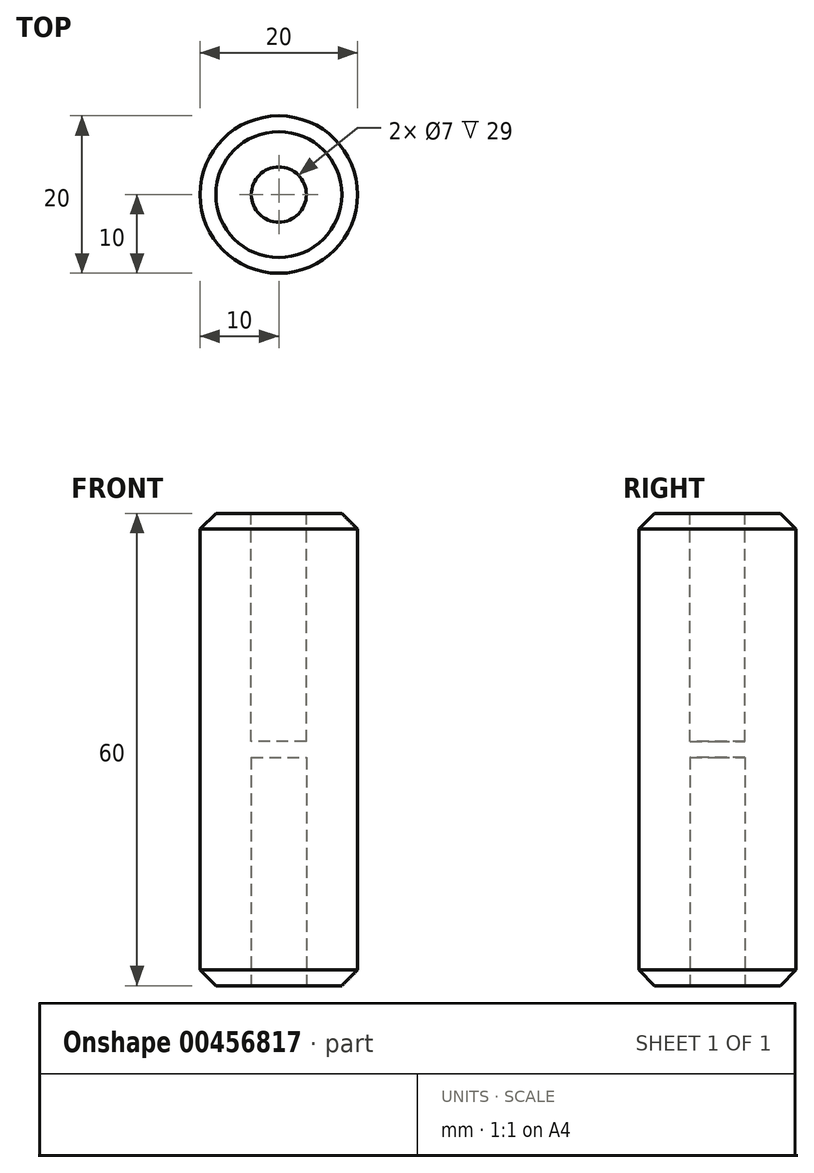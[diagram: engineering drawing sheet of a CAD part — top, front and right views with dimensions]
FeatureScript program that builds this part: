
annotation { "Feature Type Name" : "Feature", "Feature Type Description" : "" }
export const myFeature = defineFeature(function(context is Context, id is Id, definition is map)
    precondition{}
    {
        {
            var Q0;
            Q0=qCreatedBy(makeId("Top.planeOp"),FACE);
            var sketch = newSketch(context, id + "F0", { "sketchPlane" : qUnion([Q0])});
            skCircle(sketch, "E0", {"center": v(0, 0) * mm, "radius": 10 * mm});
            skSolve(sketch);
        }
        {
            var Q0;
            Q0=makeQuery(id+"F0.imprint","IMPRINT",FACE,{"disambiguationData":[TD([[makeQuery(id+"F0.imprint","IMPRINT",EDGE,{"derivedFrom":sQuery(id+"F0.wireOp",EDGE,"E0")}),1.0]])]});
            extrude(context, id + "F1", {"entities" : qUnion([Q0]), "endBound" : BoundingType.SYMMETRIC, "depth" : 60 * mm});
        }
        {
            var Q0;
            Q0=makeQuery(id+"F1.opExtrude","CAP_FACE",FACE,{"disambiguationData":[OSD([sQuery(id+"F0.wireOp",EDGE,"E0")])],"isStart":false});
            var sketch = newSketch(context, id + "F2", { "sketchPlane" : qUnion([Q0])});
            skCircle(sketch, "E1", {"center": v(0, 0) * mm, "radius": 3.5 * mm});
            skSolve(sketch);
        }
        {
            var Q0;
            Q0=makeQuery(id+"F1.opExtrude","CAP_FACE",FACE,{"disambiguationData":[OSD([sQuery(id+"F0.wireOp",EDGE,"E0")])],"isStart":true});
            var sketch = newSketch(context, id + "F3", { "sketchPlane" : qUnion([Q0])});
            skCircle(sketch, "E2", {"center": v(0, 0) * mm, "radius": 3.5 * mm});
            skSolve(sketch);
        }
        {
            var Q0;
            Q0 = qSketchRegion(id + "F2", true);
            extrude(context, id + "F4", {"entities" : qUnion([Q0]), "operationType" : NewBodyOperationType.REMOVE, "oppositeDirection" : true, "depth" : 29 * mm});
        }
        {
            var Q0;
            Q0=makeQuery(id+"F3.imprint","IMPRINT",FACE,{"disambiguationData":[TD([[makeQuery(id+"F3.imprint","IMPRINT",EDGE,{"derivedFrom":sQuery(id+"F3.wireOp",EDGE,"E2")}),1.0]])]});
            extrude(context, id + "F5", {"entities" : qUnion([Q0]), "operationType" : NewBodyOperationType.REMOVE, "oppositeDirection" : true, "depth" : 29 * mm});
        }
        {
            var Q0;
            Q0=makeQuery(id+"F1.opExtrude","CAP_EDGE",EDGE,{"disambiguationData":[OSD([sQuery(id+"F0.wireOp",EDGE,"E0")])],"isStart":false});
            var Q1;
            Q1=makeQuery(id+"F1.opExtrude","CAP_EDGE",EDGE,{"disambiguationData":[OSD([sQuery(id+"F0.wireOp",EDGE,"E0")])],"isStart":true});
            chamfer(context, id + "F6", {"entities" : qUnion([Q0, Q1]), "width" : 2 * mm, "tangentPropagation" : true});
        }
    });
